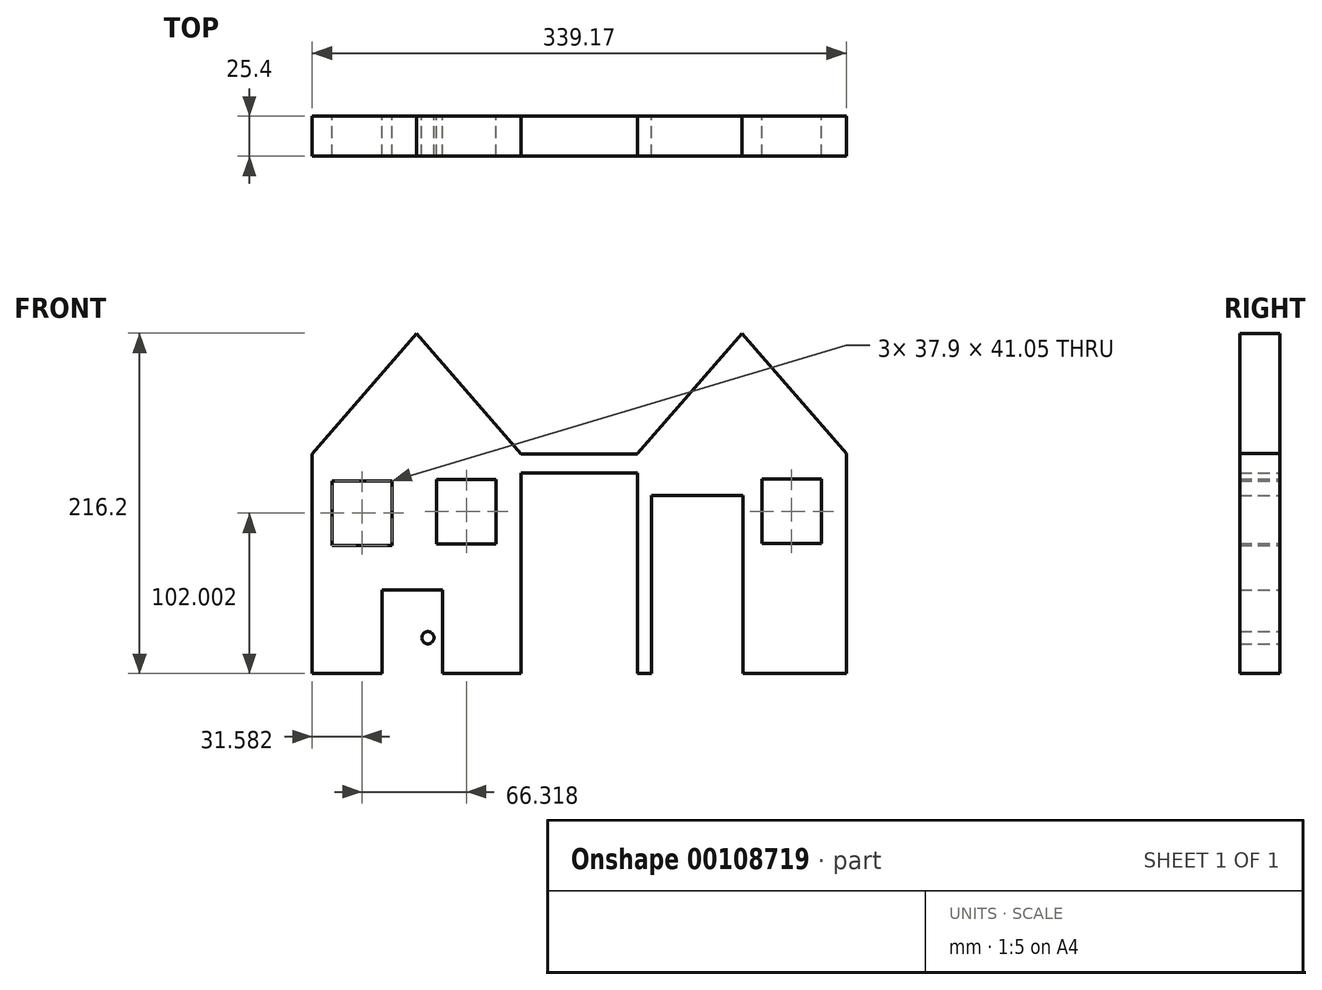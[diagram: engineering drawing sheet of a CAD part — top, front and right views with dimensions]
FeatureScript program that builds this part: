
annotation { "Feature Type Name" : "Feature", "Feature Type Description" : "" }
export const myFeature = defineFeature(function(context is Context, id is Id, definition is map)
    precondition{}
    {
        {
            var Q0;
            Q0=qCreatedBy(makeId("Front.planeOp"),FACE);
            var sketch = newSketch(context, id + "F0", { "sketchPlane" : qUnion([Q0])});
            skLineSegment(sketch, "E0.bottom", {"start": v(-66.32, 69.8) * mm, "end": v(66.32, 69.8) * mm});
            skLineSegment(sketch, "E0.top", {"start": v(-66.32, -69.8) * mm, "end": v(66.32, -69.8) * mm});
            skLineSegment(sketch, "E0.left", {"start": v(-66.32, 69.8) * mm, "end": v(-66.32, -69.8) * mm});
            skLineSegment(sketch, "E0.right", {"start": v(66.32, 69.8) * mm, "end": v(66.32, -69.8) * mm});
            skPoint(sketch, "E0.middle", {"position": v(0, 0) * mm});
            skLineSegment(sketch, "E1", {"start": v(-66.32, 69.8) * mm, "end": v(0, 146.22) * mm});
            skLineSegment(sketch, "E2", {"start": v(66.32, 69.8) * mm, "end": v(0, 146.22) * mm});
            skLineSegment(sketch, "E3", {"start": v(-22.1, -69.8) * mm, "end": v(-22.1, -16.74) * mm});
            skLineSegment(sketch, "E4", {"start": v(16.42, -69.8) * mm, "end": v(16.42, -16.74) * mm});
            skLineSegment(sketch, "E5", {"start": v(-22.1, -16.74) * mm, "end": v(16.42, -16.74) * mm});
            skCircle(sketch, "E6", {"center": v(7.1, -46.98) * mm, "radius": 3.87 * mm});
            skPoint(sketch, "E6.first.point", {"position": v(8.21, -43.26) * mm});
            skPoint(sketch, "E6.first.point.positionSnap0", {"position": v(16.42, -43.26) * mm});
            skPoint(sketch, "E6.second.point", {"position": v(6.95, -50.84) * mm});
            skPoint(sketch, "E6.third.point", {"position": v(10.74, -48.32) * mm});
            skLineSegment(sketch, "E7.bottom", {"start": v(-53.69, 52.74) * mm, "end": v(-15.8, 52.74) * mm});
            skLineSegment(sketch, "E7.top", {"start": v(-53.69, 11.68) * mm, "end": v(-15.8, 11.68) * mm});
            skLineSegment(sketch, "E7.left", {"start": v(-53.69, 52.74) * mm, "end": v(-53.69, 11.68) * mm});
            skLineSegment(sketch, "E7.right", {"start": v(-15.8, 52.74) * mm, "end": v(-15.8, 11.68) * mm});
            skLineSegment(sketch, "E8.bottom", {"start": v(12.63, 53.69) * mm, "end": v(50.53, 53.69) * mm});
            skLineSegment(sketch, "E8.top", {"start": v(12.63, 12.63) * mm, "end": v(50.53, 12.63) * mm});
            skLineSegment(sketch, "E8.left", {"start": v(12.63, 53.69) * mm, "end": v(12.63, 12.63) * mm});
            skLineSegment(sketch, "E8.right", {"start": v(50.53, 53.69) * mm, "end": v(50.53, 12.63) * mm});
            skLineSegment(sketch, "E9.left", {"start": v(66.32, 69.8) * mm, "end": v(66.32, 69.8) * mm});
            skLineSegment(sketch, "E10.left", {"start": v(66.32, 57.16) * mm, "end": v(66.32, 57.16) * mm});
            skLineSegment(sketch, "E11.bottom", {"start": v(66.32, 69.8) * mm, "end": v(140.22, 69.8) * mm});
            skLineSegment(sketch, "E11.top", {"start": v(66.32, 57.8) * mm, "end": v(140.22, 57.8) * mm});
            skLineSegment(sketch, "E11.left", {"start": v(66.32, 69.8) * mm, "end": v(66.32, 57.8) * mm});
            skLineSegment(sketch, "E11.right", {"start": v(140.22, 69.8) * mm, "end": v(140.22, 57.8) * mm});
            skLineSegment(sketch, "E12.bottom", {"start": v(140.22, 69.98) * mm, "end": v(272.85, 69.98) * mm});
            skLineSegment(sketch, "E12.top", {"start": v(140.22, -69.6) * mm, "end": v(272.85, -69.6) * mm});
            skLineSegment(sketch, "E12.left", {"start": v(140.22, 69.98) * mm, "end": v(140.22, -69.6) * mm});
            skLineSegment(sketch, "E12.right", {"start": v(272.85, 69.98) * mm, "end": v(272.85, -69.6) * mm});
            skLineSegment(sketch, "E13", {"start": v(140.22, 69.98) * mm, "end": v(206.53, 146.4) * mm});
            skLineSegment(sketch, "E14", {"start": v(272.85, 69.98) * mm, "end": v(206.53, 146.4) * mm});
            skLineSegment(sketch, "E15.bottom", {"start": v(219.17, 53.88) * mm, "end": v(257.06, 53.88) * mm});
            skLineSegment(sketch, "E15.top", {"start": v(219.17, 12.82) * mm, "end": v(257.06, 12.82) * mm});
            skLineSegment(sketch, "E15.left", {"start": v(219.17, 53.88) * mm, "end": v(219.17, 12.82) * mm});
            skLineSegment(sketch, "E15.right", {"start": v(257.06, 53.88) * mm, "end": v(257.06, 12.82) * mm});
            skLineSegment(sketch, "E16", {"start": v(149.06, -69.6) * mm, "end": v(149.06, 43.26) * mm});
            skLineSegment(sketch, "E17", {"start": v(149.06, 43.26) * mm, "end": v(207.17, 43.26) * mm});
            skLineSegment(sketch, "E18", {"start": v(207.17, 43.26) * mm, "end": v(207.17, -69.6) * mm});
            skSolve(sketch);
        }
        {
            var Q0;
            Q0=makeQuery(id+"F0.imprint","IMPRINT",FACE,{"disambiguationData":[TD([[makeQuery(id+"F0.imprint","IMPRINT",EDGE,{"derivedFrom":sQuery(id+"F0.wireOp",EDGE,"E0.bottom")}),-1.0]])]});
            var Q1;
            Q1=makeQuery(id+"F0.imprint","IMPRINT",FACE,{"disambiguationData":[TD([[makeQuery(id+"F0.imprint","IMPRINT",EDGE,{"derivedFrom":sQuery(id+"F0.wireOp",EDGE,"E6")}),1.0]])]});
            var Q2;
            Q2=makeQuery(id+"F0.imprint","IMPRINT",FACE,{"disambiguationData":[TD([[makeQuery(id+"F0.imprint","IMPRINT",EDGE,{"derivedFrom":sQuery(id+"F0.wireOp",EDGE,"E0.bottom")}),1.0]])]});
            var Q3;
            Q3=makeQuery(id+"F0.imprint","IMPRINT",FACE,{"disambiguationData":[TD([[makeQuery(id+"F0.imprint","IMPRINT",EDGE,{"derivedFrom":sQuery(id+"F0.wireOp",EDGE,"E12.bottom")}),-1.0]])]});
            var Q4;
            Q4=makeQuery(id+"F0.imprint","IMPRINT",FACE,{"disambiguationData":[TD([[makeQuery(id+"F0.imprint","IMPRINT",EDGE,{"derivedFrom":sQuery(id+"F0.wireOp",EDGE,"E12.bottom")}),1.0]])]});
            var Q5;
            Q5=makeQuery(id+"F0.imprint","IMPRINT",FACE,{"disambiguationData":[TD([[makeQuery(id+"F0.imprint","IMPRINT",EDGE,{"derivedFrom":sQuery(id+"F0.wireOp",EDGE,"E11.bottom")}),-1.0]])]});
            extrude(context, id + "F1", {"entities" : qUnion([Q0, Q1, Q2, Q3, Q4, Q5]), "depth" : 25.4 * mm});
        }
    });
